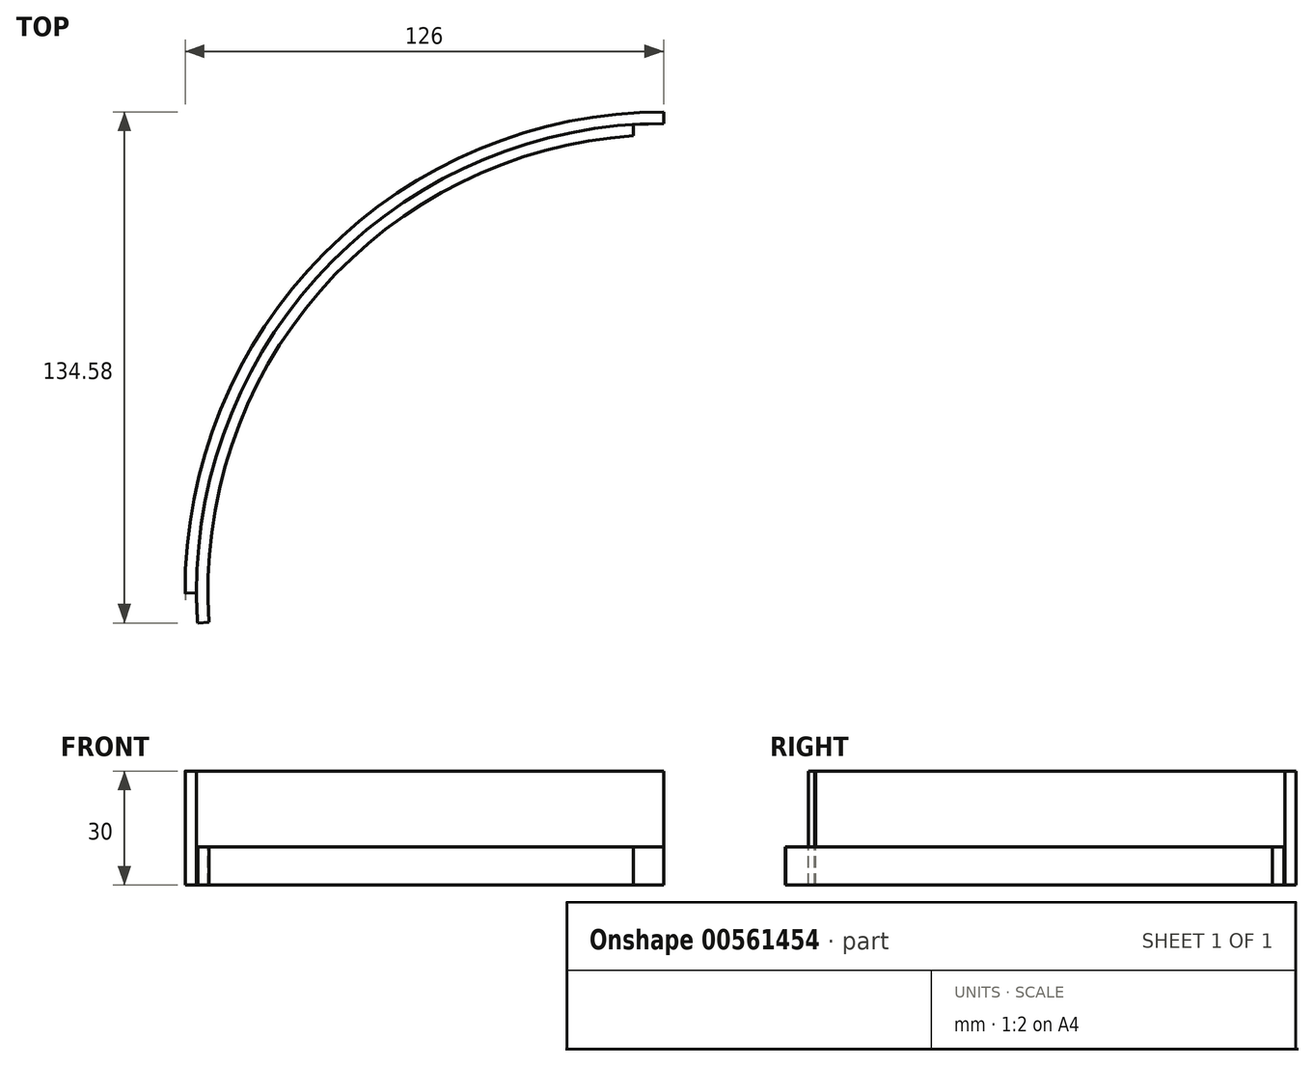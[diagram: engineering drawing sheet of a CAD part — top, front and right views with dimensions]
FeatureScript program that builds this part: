
annotation { "Feature Type Name" : "Feature", "Feature Type Description" : "" }
export const myFeature = defineFeature(function(context is Context, id is Id, definition is map)
    precondition{}
    {
        {
            var Q0;
            Q0=qCreatedBy(makeId("Top.planeOp"),FACE);
            var sketch = newSketch(context, id + "F0", { "sketchPlane" : qUnion([Q0])});
            skLineSegment(sketch, "E0", {"start": v(0, 155.82) * mm, "end": v(0, -111.27) * mm, "construction": true});
            skLineSegment(sketch, "E1", {"start": v(86.42, 0) * mm, "end": v(-216.49, 0) * mm, "construction": true});
            skLineSegment(sketch, "E2", {"start": v(0, 0) * mm, "end": v(-10.93, 156.26) * mm, "construction": true});
            skLineSegment(sketch, "E3", {"start": v(0, 0) * mm, "end": v(-216.06, -15.1) * mm, "construction": true});
            skArc(sketch, "E4", {"start": v(0, 120) * mm, "mid": v(-87.76, 81.84) * mm, "end": v(-119.7, -8.37) * mm});
            skArc(sketch, "E5", {"start": v(0, 126) * mm, "mid": v(-92.15, 85.93) * mm, "end": v(-125.7, -8.79) * mm});
            skLineSegment(sketch, "E6", {"start": v(0, 120) * mm, "end": v(0, 126) * mm});
            skLineSegment(sketch, "E7", {"start": v(-119.7, -8.37) * mm, "end": v(-125.7, -8.79) * mm});
            skSolve(sketch);
        }
        {
            var Q0;
            Q0=makeQuery(id+"F0.imprint","IMPRINT",FACE,{"disambiguationData":[TD([[makeQuery(id+"F0.imprint","IMPRINT",EDGE,{"derivedFrom":sQuery(id+"F0.wireOp",EDGE,"E4")}),-1.0]])]});
            extrude(context, id + "F1", {"entities" : qUnion([Q0]), "oppositeDirection" : true, "depth" : 30 * mm, "offsetDistance" : 25 * mm});
        }
        {
            var Q0;
            Q0=makeQuery(id+"F1.opExtrude","CAP_FACE",FACE,{"disambiguationData":[OSD([sQuery(id+"F0.wireOp",EDGE,"E4"),sQuery(id+"F0.wireOp",EDGE,"E5"),sQuery(id+"F0.wireOp",EDGE,"E6"),sQuery(id+"F0.wireOp",EDGE,"E7")])],"isStart":true});
            var sketch = newSketch(context, id + "F2", { "sketchPlane" : qUnion([Q0])});
            skArc(sketch, "E8", {"start": v(0, 120) * mm, "mid": v(-87.76, 81.84) * mm, "end": v(-119.7, -8.37) * mm});
            skArc(sketch, "E9", {"start": v(0, 123) * mm, "mid": v(-89.96, 83.89) * mm, "end": v(-122.7, -8.58) * mm});
            skLineSegment(sketch, "E10", {"start": v(0, 123) * mm, "end": v(0, 120) * mm});
            skLineSegment(sketch, "E11", {"start": v(-122.7, -8.58) * mm, "end": v(-119.7, -8.37) * mm});
            skSolve(sketch);
        }
        {
            var Q0;
            Q0=makeQuery(id+"F2.imprint","IMPRINT",FACE,{"disambiguationData":[TD([[makeQuery(id+"F2.imprint","IMPRINT",EDGE,{"derivedFrom":sQuery(id+"F2.wireOp",EDGE,"E8")}),-1.0]])]});
            extrude(context, id + "F3", {"entities" : qUnion([Q0]), "operationType" : NewBodyOperationType.REMOVE, "oppositeDirection" : true, "depth" : 20 * mm, "offsetDistance" : 25 * mm});
        }
        {
            var Q0;
            Q0=makeQuery(id+"F1.opExtrude","CAP_FACE",FACE,{"disambiguationData":[OSD([sQuery(id+"F0.wireOp",EDGE,"E4"),sQuery(id+"F0.wireOp",EDGE,"E5"),sQuery(id+"F0.wireOp",EDGE,"E6"),sQuery(id+"F0.wireOp",EDGE,"E7")])],"isStart":true});
            var sketch = newSketch(context, id + "F4", { "sketchPlane" : qUnion([Q0])});
            skLineSegment(sketch, "E12", {"start": v(0, 0) * mm, "end": v(0, 126.78) * mm, "construction": true});
            skLineSegment(sketch, "E13", {"start": v(0, 0) * mm, "end": v(-9.2, 131.54) * mm, "construction": true});
            skLineSegment(sketch, "E14", {"start": v(-125.9, -8.8) * mm, "end": v(-122.7, -8.58) * mm});
            skLineSegment(sketch, "E15", {"start": v(-122.7, -8.58) * mm, "end": v(-123, -0.59) * mm});
            skLineSegment(sketch, "E16", {"start": v(-123, -0.59) * mm, "end": v(-126, -0.8) * mm});
            skLineSegment(sketch, "E17", {"start": v(-126, -0.8) * mm, "end": v(-125.9, -8.8) * mm});
            skSolve(sketch);
        }
        {
            var Q0;
            {var subQ0=sQuery(id+"F4.wireOp",EDGE,"E14");Q0=makeQuery(id+"F4.imprint","IMPRINT",FACE,{"disambiguationData":[TD([[makeQuery(id+"F4.imprint","IMPRINT",EDGE,{"derivedFrom":subQ0}),-1.0]])]});}
            extrude(context, id + "F5", {"entities" : qUnion([Q0]), "operationType" : NewBodyOperationType.REMOVE, "oppositeDirection" : true, "depth" : 30 * mm, "offsetDistance" : 25 * mm});
        }
        {
            var Q0;
            Q0=makeQuery(id+"F3.boolean.opBoolean","COPY",FACE,{"derivedFrom":makeQuery(id+"F3.opExtrude","CAP_FACE",FACE,{"disambiguationData":[OSD([sQuery(id+"F2.wireOp",EDGE,"E8"),sQuery(id+"F2.wireOp",EDGE,"E9"),sQuery(id+"F2.wireOp",EDGE,"E10"),sQuery(id+"F2.wireOp",EDGE,"E11")])],"isStart":false})});
            var sketch = newSketch(context, id + "F6", { "sketchPlane" : qUnion([Q0])});
            skLineSegment(sketch, "E18", {"start": v(0, 120) * mm, "end": v(-8, 119.73) * mm});
            skLineSegment(sketch, "E19", {"start": v(-8, 119.73) * mm, "end": v(-8, 122.74) * mm});
            skLineSegment(sketch, "E20", {"start": v(-8, 122.74) * mm, "end": v(0, 123) * mm});
            skLineSegment(sketch, "E21", {"start": v(0, 123) * mm, "end": v(0, 120) * mm});
            skSolve(sketch);
        }
        {
            var Q0;
            {var subQ0=sQuery(id+"F6.wireOp",EDGE,"E19");Q0=makeQuery(id+"F6.imprint","IMPRINT",FACE,{"disambiguationData":[TD([[makeQuery(id+"F6.imprint","IMPRINT",EDGE,{"derivedFrom":subQ0}),-1.0]])]});}
            extrude(context, id + "F7", {"entities" : qUnion([Q0]), "operationType" : NewBodyOperationType.REMOVE, "oppositeDirection" : true, "depth" : 10 * mm, "offsetDistance" : 25 * mm});
        }
    });
